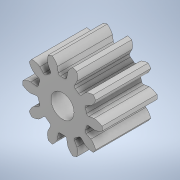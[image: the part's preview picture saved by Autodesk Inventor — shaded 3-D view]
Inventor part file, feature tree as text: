
AUTODESK INVENTOR PART (.ipt)
format: ipt  version: 2022.3 (Build 263350000, 350)  size: 261,120 bytes
history: mixed  units: in
note: dims shown in document units (in); Inventor stores cm internally (conversion verified against a paired STEP export)
features: extrude x1, sketch x1, imported_body x1
ambient origin geometry x8: Origin, YZ Plane, XZ Plane, XY Plane, X Axis, Y Axis, Z Axis, Center Point
bodies: Solid1 (imported_parasolid), Body1 (imported_parasolid)
feature tree (3):
  extrude  "Extrusion1"  TaperAngle=0.0deg  [1 undecoded]
  sketch  "Sketch1"  dims[d0=0.1654in d1=0.0in d2=0.0in]
  imported_body  NMx_Import_Brep_tag  [imported B-rep: ~14 faces, bbox_mm=[6.420511, 3.424465, 10.0]]
note: 1 required parameter value undecoded (feature->parameter linkage not recoverable at this tier; creation-order binding heuristic only, values carry confidence <= 0.55)
